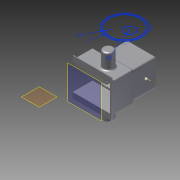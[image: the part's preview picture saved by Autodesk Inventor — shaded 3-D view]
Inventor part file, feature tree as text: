
AUTODESK INVENTOR PART (.ipt)
format: ipt  version: 2012 (Build 160160000, 160)  size: 956,416 bytes
history: native  units: mm
features: sketch x34, extrude x34, reference x30, projected_geometry x24, fillet x13, plane x5, other x2
ambient origin geometry x8: Origin, YZ Plane, XZ Plane, XY Plane, X Axis, Y Axis, Z Axis, Center Point
bodies: Solid1 (feature_tree)
feature tree (142):
  plane  "Work Plane2"
  sketch  "Sketch3"  dims[d1=0.3mm d2=0.3mm]
  plane  "Work Plane3"
  extrude  "Extrusion1"  Depth=0.3mm
  extrude  "Extrusion2"  Depth=10.0mm TaperAngle=0.0deg
  plane  "Work Plane4"
  extrude  "Extrusion3"  Depth=10.0mm TaperAngle=0.0deg
  extrude  "Extrusion4"  Depth=2.0mm
  extrude  "Extrusion5"  Depth=2.0mm
  extrude  "Extrusion6"  Depth=2.0mm TaperAngle=0.0deg
  extrude  "Extrusion7"  TaperAngle=0.0deg  [1 undecoded]
  extrude  "Extrusion8"  TaperAngle=0.0deg  [1 undecoded]
  fillet  "Fillet3"  Radius=20.0mm
  fillet  "Fillet4"  Radius=20.0mm
  fillet  "Fillet5"  Radius=0.3mm
  extrude  "Extrusion10"  Depth=0.3mm
  extrude  "Extrusion11"  Depth=0.3mm TaperAngle=0.0deg
  extrude  "Extrusion12"  Depth=1.0mm
  extrude  "Extrusion13"  Depth=2.0mm TaperAngle=0.0deg
  extrude  "Extrusion14"  Depth=0.3mm
  extrude  "Extrusion15"  Depth=0.3mm
  extrude  "Extrusion16"  TaperAngle=0.0deg  [1 undecoded]
  extrude  "Extrusion17"  Depth=2.0mm
  extrude  "Extrusion18"  Depth=2.0mm TaperAngle=0.0deg
  extrude  "Extrusion20"  Depth=14.0mm
  extrude  "Extrusion21"  Depth=7.0mm TaperAngle=0.0deg
  plane  "Work Plane5"
  extrude  "Extrusion22"  Depth=3.3mm
  extrude  "Extrusion23"  Depth=3.3mm
  extrude  "Extrusion24"  Depth=0.3mm
  extrude  "Extrusion25"  Depth=0.3mm
  plane  "Work Plane7"
  extrude  "Extrusion26"  Depth=20.0mm TaperAngle=0.0deg
  extrude  "Extrusion27"  Depth=0.3mm
  extrude  "Extrusion28"  Depth=0.3mm
  extrude  "Extrusion29"  Depth=2.0mm
  extrude  "Extrusion30"  Depth=2.0mm
  extrude  "Extrusion31"  TaperAngle=45.0deg  [1 undecoded]
  extrude  "Extrusion34"  Depth=9.0mm
  other  "Work Axis1"
  fillet  "Fillet47"  Radius=10.0mm
  fillet  "Fillet48"  [1 undecoded]
  fillet  "Fillet49"  Radius=10.0mm
  fillet  "Fillet50"  Radius=10.0mm
  fillet  "Fillet51"  Radius=10.0mm
  fillet  "Fillet52"  Radius=0.3mm
  fillet  "Fillet54"  Radius=0.3mm
  fillet  "Fillet55"  Radius=10.0mm
  other  "Work Axis3"
  extrude  "Extrusion35"  Depth=10.0mm TaperAngle=0.0deg
  extrude  "Extrusion36"  Depth=10.0mm TaperAngle=0.0deg
  extrude  "Extrusion37"  Depth=25.4mm TaperAngle=0.0deg
  extrude  "Extrusion38"  Depth=2.0mm
  fillet  "Fillet56"  Radius=2.0mm
  fillet  "Fillet57"  Radius=2.0mm
  reference  "Reference32"
  sketch  "Sketch4"  dims[d3=2.0mm d4=10.0mm d5=0.0mm]
  reference  "Reference33"
  sketch  "Sketch5"  dims[d6=0.3mm d7=10.0mm d8=0.0mm]
  sketch  "Sketch7"  dims[d9=2.0mm d10=2.0mm]
  projected_geometry  "Projected Loop3"
  sketch  "Sketch8"  dims[d11=2.0mm d12=2.0mm]
  sketch  "Sketch10"  dims[d13=120.0mm d14=2.0mm d15=0.0mm]
  reference  "Reference36"
  sketch  "Sketch11"  dims[d24=2.0mm d25=0.0mm]
  reference  "Reference37"
  sketch  "Sketch12"  dims[d26=2.0mm d27=0.0mm d28=20.0mm d29=0.0mm d31=20.0mm d32=0.0mm d34=0.3mm]
  sketch  "Sketch15"  dims[d35=20.0mm d36=0.0mm d37=0.3mm]
  projected_geometry  "Projected Loop5"
  projected_geometry  "Projected Loop6"
  sketch  "Sketch16"  dims[d38=10.0mm d39=0.0mm d40=0.3mm d41=0.0mm]
  reference  "Reference46"
  reference  "Reference47"
  reference  "Reference48"
  reference  "Reference49"
  reference  "Reference50"
  reference  "Reference51"
  reference  "Reference52"
  reference  "Reference53"
  sketch  "Sketch17"  dims[d43=1.0mm d44=1.0mm]
  reference  "Reference54"
  reference  "Reference55"
  reference  "Reference56"
  reference  "Reference57"
  reference  "Reference58"
  reference  "Reference59"
  reference  "Reference60"
  reference  "Reference61"
  sketch  "Sketch18"  dims[d45=1.0mm d52=2.0mm d53=0.0mm]
  reference  "Reference62"
  sketch  "Sketch19"  dims[d58=2.0mm d59=0.0mm d60=0.3mm]
  projected_geometry  "Projected Loop7"
  projected_geometry  "Projected Loop8"
  sketch  "Sketch20"  dims[d61=0.3mm d62=0.3mm]
  projected_geometry  "Projected Loop9"
  projected_geometry  "Projected Loop10"
  sketch  "Sketch21"  dims[d63=0.3mm d64=0.0mm]
  projected_geometry  "Projected Loop11"
  sketch  "Sketch22"  dims[d66=0.0mm d67=2.0mm]
  reference  "Reference63"
  reference  "Reference64"
  reference  "Reference65"
  reference  "Reference66"
  reference  "Reference67"
  reference  "Reference68"
  reference  "Reference69"
  reference  "Reference70"
  sketch  "Sketch23"  dims[d68=2.0mm d69=2.0mm d70=0.0mm]
  projected_geometry  "Projected Loop12"
  projected_geometry  "Projected Loop13"
  projected_geometry  "Projected Loop14"
  projected_geometry  "Projected Loop15"
  sketch  "Sketch25"  dims[d72=2.0mm d73=0.0mm d74=14.0mm]
  projected_geometry  "Projected Loop16"
  sketch  "Sketch26"  dims[d78=2.0mm d79=0.0mm d80=7.0mm d81=0.0mm]
  sketch  "Sketch28"  dims[d82=10.0mm d83=0.0mm d84=3.3mm]
  projected_geometry  "Projected Loop21"
  sketch  "Sketch29"  dims[d85=3.3mm d86=3.3mm]
  projected_geometry  "Projected Loop22"
  projected_geometry  "Projected Loop23"
  sketch  "Sketch30"  dims[d87=3.3mm d88=0.3mm]
  projected_geometry  "Projected Loop24"
  sketch  "Sketch31"  dims[d89=0.3mm d90=0.3mm]
  projected_geometry  "Projected Loop25"
  sketch  "Sketch32"  dims[d91=0.3mm d94=20.0mm d95=0.0mm]
  sketch  "Sketch33"  dims[d97=0.3mm d98=0.3mm]
  projected_geometry  "Projected Loop26"
  sketch  "Sketch34"  dims[d99=0.3mm d100=0.3mm]
  projected_geometry  "Projected Loop27"
  sketch  "Sketch35"  dims[d101=0.3mm d102=0.0mm d103=2.0mm]
  projected_geometry  "Projected Loop28"
  projected_geometry  "Projected Loop29"
  sketch  "Sketch37"  dims[d104=2.0mm d105=2.0mm]
  sketch  "Sketch38"  dims[d106=2.0mm d111=45.0deg]
  projected_geometry  "Projected Loop31"
  sketch  "Sketch41"  dims[d112=9.0mm d113=9.0mm d114=10.0mm d115=0.0mm d116=0.0mm d117=0.0mm d123=10.0mm d124=0.0mm d132=10.0mm d133=0.0mm d134=10.0mm d135=0.0mm d138=0.3mm d139=0.0mm d151=0.3mm d152=0.0mm d153=10.0mm d154=0.0mm]
  reference  "Reference73"
  sketch  "Sketch42"  dims[d155=10.0mm d156=0.0mm d157=10.0mm d158=0.0mm]
  sketch  "Sketch43"  dims[d159=4.0mm d160=10.0mm d161=0.0mm]
  projected_geometry  "Projected Loop33"
  sketch  "Sketch44"  dims[d162=10.0mm d163=0.0mm d186=25.4mm d187=0.0mm]
  sketch  "Sketch45"  dims[d189=1.0mm d190=2.0mm d191=2.0mm d192=2.0mm d193=2.0mm d194=1.0mm d196=2.0mm d197=1.5mm d198=108.5mm d199=0.0mm d200=1.657mm d201=0.0mm d202=35.343104mm d203=17.671552mm d204=21.697757mm d205=10.848879mm d206=12.7mm d207=19.05mm d208=0.0mm d209=19.05mm d210=0.0mm d211=2.0mm d212=2.0mm]
note: 5 required parameter values undecoded (feature->parameter linkage not recoverable at this tier; creation-order binding heuristic only, values carry confidence <= 0.55)
